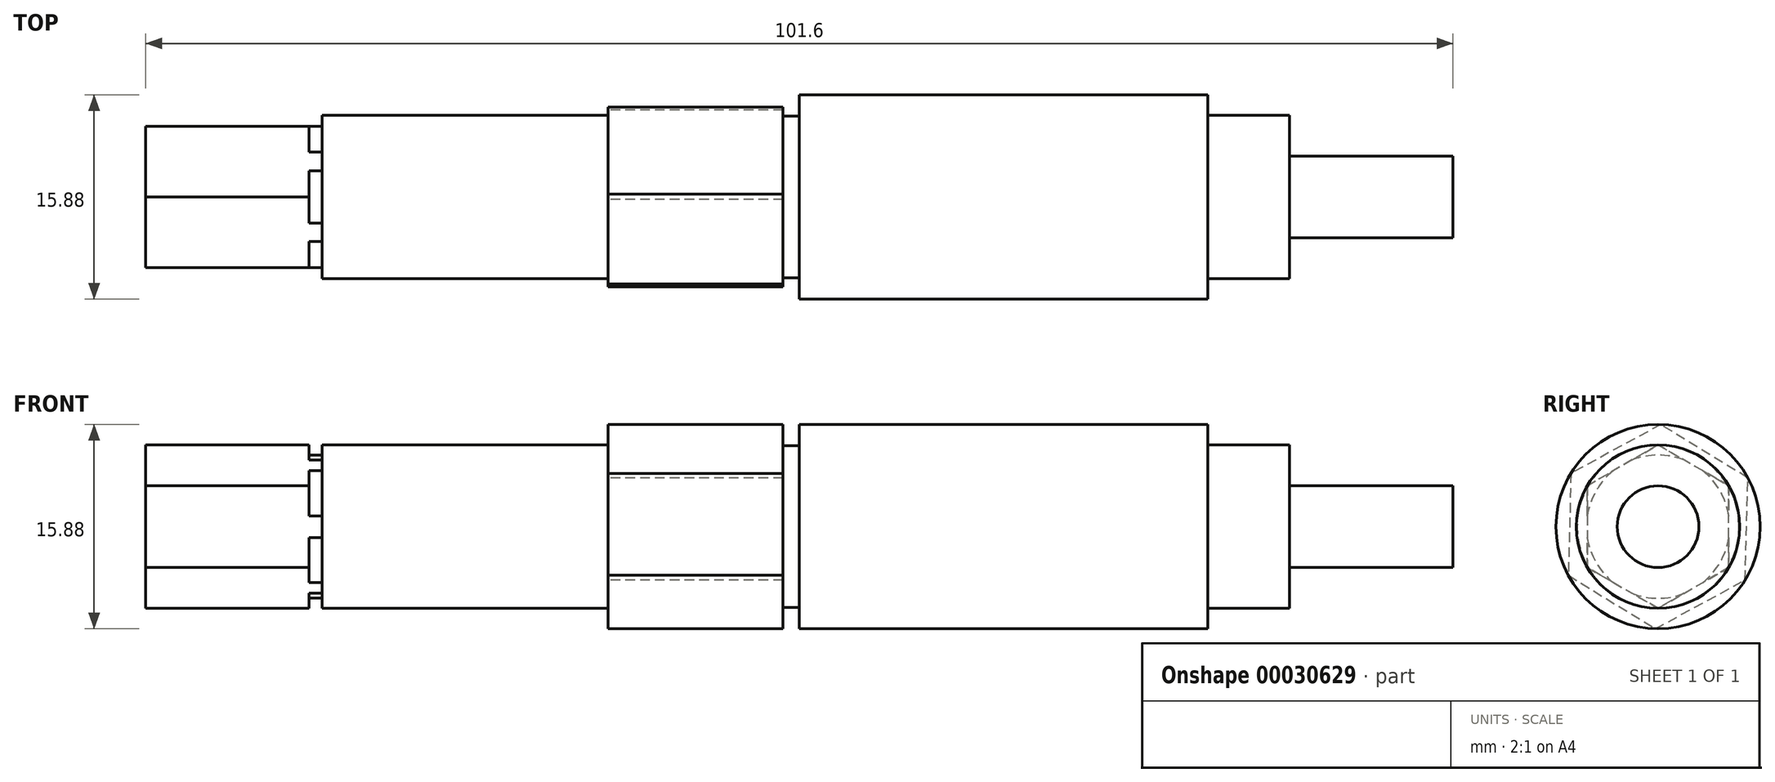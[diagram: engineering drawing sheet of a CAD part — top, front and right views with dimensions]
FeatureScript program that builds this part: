
annotation { "Feature Type Name" : "Feature", "Feature Type Description" : "" }
export const myFeature = defineFeature(function(context is Context, id is Id, definition is map)
    precondition{}
    {
        {
            var Q0;
            Q0=qCreatedBy(makeId("Front.planeOp"),FACE);
            var sketch = newSketch(context, id + "F0", { "sketchPlane" : qUnion([Q0])});
            skLineSegment(sketch, "E0", {"start": v(0, 0) * mm, "end": v(101.6, 0) * mm});
            skLineSegment(sketch, "E1", {"start": v(101.6, 0) * mm, "end": v(101.6, 3.17) * mm});
            skLineSegment(sketch, "E2", {"start": v(101.6, 3.17) * mm, "end": v(88.9, 3.17) * mm});
            skLineSegment(sketch, "E3", {"start": v(88.9, 3.17) * mm, "end": v(88.9, 6.35) * mm});
            skLineSegment(sketch, "E4", {"start": v(88.9, 6.35) * mm, "end": v(82.55, 6.35) * mm});
            skLineSegment(sketch, "E5", {"start": v(82.55, 6.35) * mm, "end": v(82.55, 7.94) * mm});
            skLineSegment(sketch, "E6", {"start": v(82.55, 7.94) * mm, "end": v(50.8, 7.94) * mm});
            skLineSegment(sketch, "E7", {"start": v(35.94, 7.94) * mm, "end": v(35.94, 6.35) * mm});
            skLineSegment(sketch, "E8", {"start": v(35.94, 6.35) * mm, "end": v(13.72, 6.35) * mm});
            skLineSegment(sketch, "E9", {"start": v(0, 6.35) * mm, "end": v(0, 0) * mm});
            skLineSegment(sketch, "E10", {"start": v(0, 6.35) * mm, "end": v(0, 45.58) * mm, "construction": true});
            skLineSegment(sketch, "E11", {"start": v(101.6, 0) * mm, "end": v(140.43, 0) * mm, "construction": true});
            skLineSegment(sketch, "E12.top", {"start": v(12.7, 5.56) * mm, "end": v(13.72, 5.56) * mm});
            skLineSegment(sketch, "E12.left", {"start": v(12.7, 6.35) * mm, "end": v(12.7, 5.56) * mm});
            skLineSegment(sketch, "E12.right", {"start": v(13.72, 6.35) * mm, "end": v(13.72, 5.56) * mm});
            skLineSegment(sketch, "E13.top", {"start": v(49.53, 6.29) * mm, "end": v(50.8, 6.29) * mm});
            skLineSegment(sketch, "E13.left", {"start": v(49.53, 7.94) * mm, "end": v(49.53, 6.29) * mm});
            skLineSegment(sketch, "E13.right", {"start": v(50.8, 7.94) * mm, "end": v(50.8, 6.29) * mm});
            skLineSegment(sketch, "E14.trimOffspring", {"start": v(12.7, 6.35) * mm, "end": v(0, 6.35) * mm});
            skLineSegment(sketch, "E15.trimOffspring", {"start": v(49.53, 7.94) * mm, "end": v(35.94, 7.94) * mm});
            skSolve(sketch);
        }
        {
            var Q0;
            Q0 = qSketchRegion(id + "F0", true);
            var Q1;
            Q1=sQuery(id+"F0.wireOp",EDGE,"E11");
            revolve(context, id + "F1", {"entities" : qUnion([Q0]), "axis" : qUnion([Q1]), "revolveType" : RevolveType.FULL});
        }
        {
            var Q0;
            Q0=makeQuery(id+"F1.opRevolve","SWEPT_FACE",FACE,{"disambiguationData":[OSD([sQuery(id+"F0.wireOp",EDGE,"E9")])]});
            var sketch = newSketch(context, id + "F2", { "sketchPlane" : qUnion([Q0])});
            skCircle(sketch, "E16.cCircle", {"center": v(0, 0) * mm, "radius": 6.35 * mm, "construction": true});
            skLineSegment(sketch, "E16.0", {"start": v(0, -6.35) * mm, "end": v(-5.5, -3.17) * mm});
            skLineSegment(sketch, "E16.1", {"start": v(-5.5, -3.17) * mm, "end": v(-5.5, 3.17) * mm});
            skLineSegment(sketch, "E16.2", {"start": v(-5.5, 3.17) * mm, "end": v(0, 6.35) * mm});
            skLineSegment(sketch, "E16.3", {"start": v(0, 6.35) * mm, "end": v(5.5, 3.17) * mm});
            skLineSegment(sketch, "E16.4", {"start": v(5.5, 3.17) * mm, "end": v(5.5, -3.17) * mm});
            skLineSegment(sketch, "E16.5", {"start": v(5.5, -3.17) * mm, "end": v(0, -6.35) * mm});
            skSolve(sketch);
        }
        {
            var Q0;
            {var subQ1=sQuery(id+"F2.wireOp",EDGE,"E16.3");Q0=makeQuery(id+"F2.imprint","IMPRINT",FACE,{"disambiguationData":[TD([[makeQuery(id+"F2.imprint","IMPRINT",EDGE,{"derivedFrom":subQ1}),1.0]])]});}
            var Q1;
            {var subQ1=sQuery(id+"F2.wireOp",EDGE,"E16.4");Q1=makeQuery(id+"F2.imprint","IMPRINT",FACE,{"disambiguationData":[TD([[makeQuery(id+"F2.imprint","IMPRINT",EDGE,{"derivedFrom":subQ1}),1.0]])]});}
            var Q2;
            {var subQ1=sQuery(id+"F2.wireOp",EDGE,"E16.5");Q2=makeQuery(id+"F2.imprint","IMPRINT",FACE,{"disambiguationData":[TD([[makeQuery(id+"F2.imprint","IMPRINT",EDGE,{"derivedFrom":subQ1}),1.0]])]});}
            var Q3;
            {var subQ1=sQuery(id+"F2.wireOp",EDGE,"E16.0");Q3=makeQuery(id+"F2.imprint","IMPRINT",FACE,{"disambiguationData":[TD([[makeQuery(id+"F2.imprint","IMPRINT",EDGE,{"derivedFrom":subQ1}),1.0]])]});}
            var Q4;
            {var subQ1=sQuery(id+"F2.wireOp",EDGE,"E16.1");Q4=makeQuery(id+"F2.imprint","IMPRINT",FACE,{"disambiguationData":[TD([[makeQuery(id+"F2.imprint","IMPRINT",EDGE,{"derivedFrom":subQ1}),1.0]])]});}
            var Q5;
            {var subQ1=sQuery(id+"F2.wireOp",EDGE,"E16.2");Q5=makeQuery(id+"F2.imprint","IMPRINT",FACE,{"disambiguationData":[TD([[makeQuery(id+"F2.imprint","IMPRINT",EDGE,{"derivedFrom":subQ1}),1.0]])]});}
            extrude(context, id + "F3", {"entities" : qUnion([Q0, Q1, Q2, Q3, Q4, Q5]), "operationType" : NewBodyOperationType.REMOVE, "oppositeDirection" : true, "depth" : 13.72 * mm});
        }
        {
            var Q0;
            Q0=makeQuery(id+"F1.opRevolve","SWEPT_FACE",FACE,{"disambiguationData":[OSD([sQuery(id+"F0.wireOp",EDGE,"E7")])]});
            var sketch = newSketch(context, id + "F4", { "sketchPlane" : qUnion([Q0])});
            skCircle(sketch, "E17.cCircle", {"center": v(0, 0) * mm, "radius": 7.94 * mm, "construction": true});
            skLineSegment(sketch, "E17.0", {"start": v(-6.77, -4.15) * mm, "end": v(-6.98, 3.79) * mm});
            skLineSegment(sketch, "E17.1", {"start": v(-6.98, 3.79) * mm, "end": v(-0.2, 7.93) * mm});
            skLineSegment(sketch, "E17.2", {"start": v(-0.2, 7.93) * mm, "end": v(6.77, 4.15) * mm});
            skLineSegment(sketch, "E17.3", {"start": v(6.77, 4.15) * mm, "end": v(6.98, -3.79) * mm});
            skLineSegment(sketch, "E17.4", {"start": v(6.98, -3.79) * mm, "end": v(0.2, -7.93) * mm});
            skLineSegment(sketch, "E17.5", {"start": v(0.2, -7.93) * mm, "end": v(-6.77, -4.15) * mm});
            skSolve(sketch);
        }
        {
            var Q0;
            {var subQ1=sQuery(id+"F4.wireOp",EDGE,"E17.3");Q0=makeQuery(id+"F4.imprint","IMPRINT",FACE,{"disambiguationData":[TD([[makeQuery(id+"F4.imprint","IMPRINT",EDGE,{"derivedFrom":subQ1}),1.0]])]});}
            var Q1;
            {var subQ1=sQuery(id+"F4.wireOp",EDGE,"E17.2");Q1=makeQuery(id+"F4.imprint","IMPRINT",FACE,{"disambiguationData":[TD([[makeQuery(id+"F4.imprint","IMPRINT",EDGE,{"derivedFrom":subQ1}),1.0]])]});}
            var Q2;
            {var subQ1=sQuery(id+"F4.wireOp",EDGE,"E17.1");Q2=makeQuery(id+"F4.imprint","IMPRINT",FACE,{"disambiguationData":[TD([[makeQuery(id+"F4.imprint","IMPRINT",EDGE,{"derivedFrom":subQ1}),1.0]])]});}
            var Q3;
            {var subQ1=sQuery(id+"F4.wireOp",EDGE,"E17.0");Q3=makeQuery(id+"F4.imprint","IMPRINT",FACE,{"disambiguationData":[TD([[makeQuery(id+"F4.imprint","IMPRINT",EDGE,{"derivedFrom":subQ1}),1.0]])]});}
            var Q4;
            {var subQ1=sQuery(id+"F4.wireOp",EDGE,"E17.4");Q4=makeQuery(id+"F4.imprint","IMPRINT",FACE,{"disambiguationData":[TD([[makeQuery(id+"F4.imprint","IMPRINT",EDGE,{"derivedFrom":subQ1}),1.0]])]});}
            var Q5;
            {var subQ1=sQuery(id+"F4.wireOp",EDGE,"E17.5");Q5=makeQuery(id+"F4.imprint","IMPRINT",FACE,{"disambiguationData":[TD([[makeQuery(id+"F4.imprint","IMPRINT",EDGE,{"derivedFrom":subQ1}),1.0]])]});}
            extrude(context, id + "F5", {"entities" : qUnion([Q0, Q1, Q2, Q3, Q4, Q5]), "operationType" : NewBodyOperationType.REMOVE, "endBound" : BoundingType.UP_TO_NEXT, "oppositeDirection" : true, "depth" : 25.4 * mm});
        }
    });
